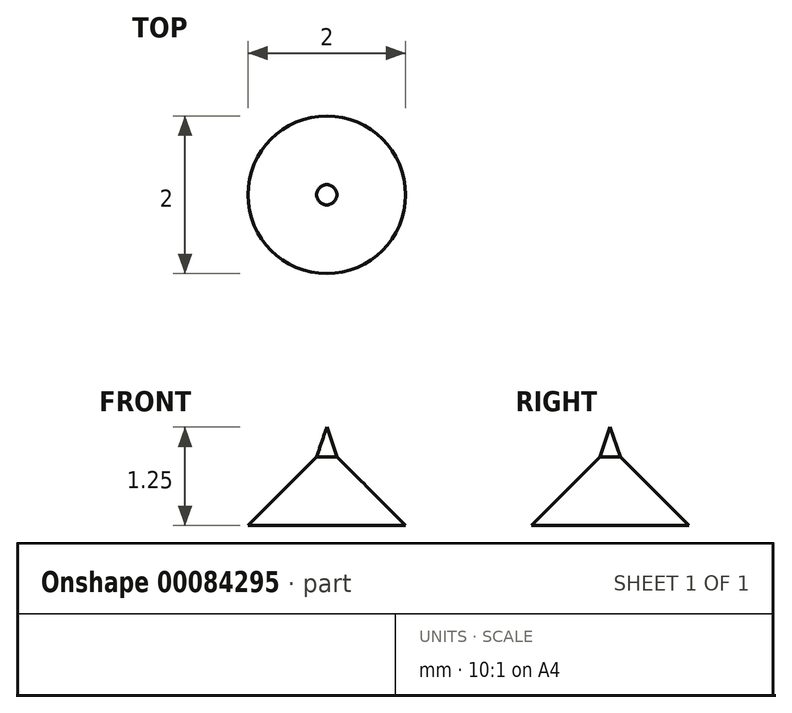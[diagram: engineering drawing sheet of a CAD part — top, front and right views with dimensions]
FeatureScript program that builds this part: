
annotation { "Feature Type Name" : "Feature", "Feature Type Description" : "" }
export const myFeature = defineFeature(function(context is Context, id is Id, definition is map)
    precondition{}
    {
        {
            var Q0;
            Q0=qCreatedBy(makeId("Front.planeOp"),FACE);
            var sketch = newSketch(context, id + "F0", { "sketchPlane" : qUnion([Q0])});
            skLineSegment(sketch, "E0", {"start": v(0, 0) * mm, "end": v(1, 0) * mm});
            skLineSegment(sketch, "E1", {"start": v(1, 0) * mm, "end": v(0, 1) * mm});
            skLineSegment(sketch, "E2", {"start": v(0, 1) * mm, "end": v(0, 0) * mm});
            skLineSegment(sketch, "E3", {"start": v(0, 1) * mm, "end": v(0, 1.25) * mm});
            skLineSegment(sketch, "E4", {"start": v(0, 1.25) * mm, "end": v(0.13, 0.87) * mm});
            skSolve(sketch);
        }
        {
            var Q0;
            {var subQ0=sQuery(id+"F0.wireOp",EDGE,"E0");Q0=makeQuery(id+"F0.imprint","IMPRINT",FACE,{"disambiguationData":[TD([[makeQuery(id+"F0.imprint","IMPRINT",EDGE,{"derivedFrom":subQ0}),1.0]])]});}
            var Q1;
            {var subQ0=sQuery(id+"F0.wireOp",EDGE,"E3");Q1=makeQuery(id+"F0.imprint","IMPRINT",FACE,{"disambiguationData":[TD([[makeQuery(id+"F0.imprint","IMPRINT",EDGE,{"derivedFrom":subQ0}),-1.0]])]});}
            var Q2;
            Q2=sQuery(id+"F0.wireOp",EDGE,"E2");
            revolve(context, id + "F1", {"entities" : qUnion([Q0, Q1]), "axis" : qUnion([Q2]), "revolveType" : RevolveType.FULL});
        }
    });
